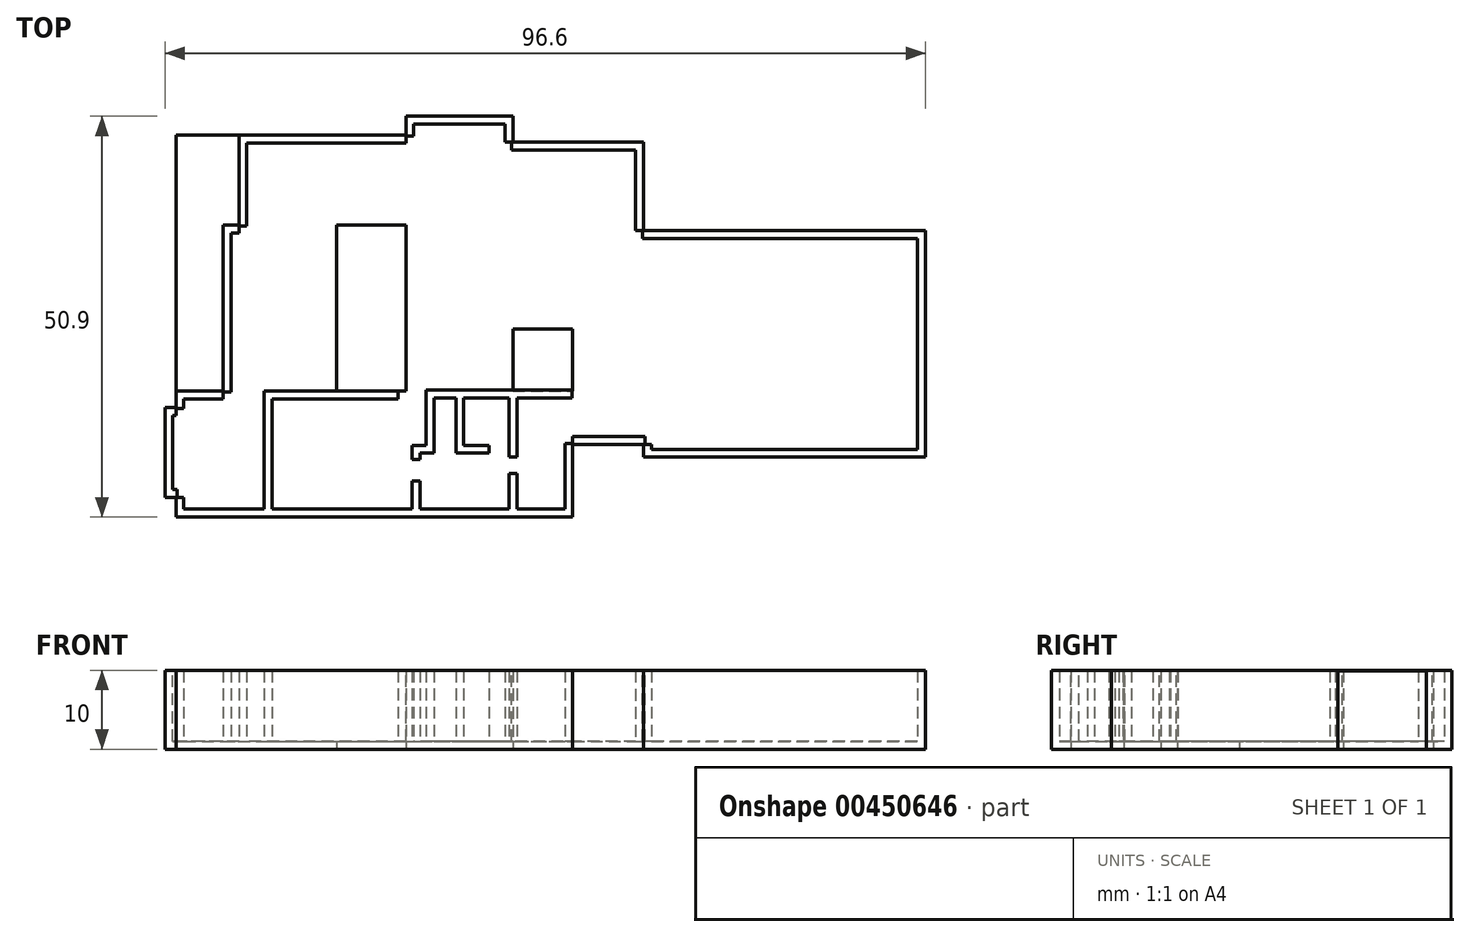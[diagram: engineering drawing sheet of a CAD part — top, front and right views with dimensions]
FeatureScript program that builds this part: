
annotation { "Feature Type Name" : "Feature", "Feature Type Description" : "" }
export const myFeature = defineFeature(function(context is Context, id is Id, definition is map)
    precondition{}
    {
        {
            var Q0;
            Q0=qCreatedBy(makeId("Top.planeOp"),FACE);
            var sketch = newSketch(context, id + "F0", { "sketchPlane" : qUnion([Q0])});
            skLineSegment(sketch, "E0.bottom", {"start": v(-51.63, -21.6) * mm, "end": v(-40.43, -21.6) * mm});
            skLineSegment(sketch, "E0.top", {"start": v(-51.63, -37.6) * mm, "end": v(-40.43, -37.6) * mm});
            skLineSegment(sketch, "E0.left", {"start": v(-51.63, -21.6) * mm, "end": v(-51.63, -37.6) * mm});
            skLineSegment(sketch, "E0.right", {"start": v(-40.43, -21.6) * mm, "end": v(-40.43, -37.6) * mm});
            skPoint(sketch, "E1.firstSnap0", {"position": v(-46.03, -21.6) * mm});
            skPoint(sketch, "E1.oppositeSnap0", {"position": v(-40.43, -29.6) * mm});
            skLineSegment(sketch, "E2.bottom", {"start": v(-51.63, -23.72) * mm, "end": v(-53.03, -23.72) * mm});
            skLineSegment(sketch, "E2.top", {"start": v(-51.63, -35.12) * mm, "end": v(-53.03, -35.12) * mm});
            skLineSegment(sketch, "E2.left", {"start": v(-51.63, -23.72) * mm, "end": v(-51.63, -35.12) * mm});
            skLineSegment(sketch, "E2.right", {"start": v(-53.03, -23.72) * mm, "end": v(-53.03, -35.12) * mm});
            skLineSegment(sketch, "E3.bottom", {"start": v(-45.63, -21.6) * mm, "end": v(-31.23, -21.6) * mm});
            skLineSegment(sketch, "E3.top", {"start": v(-45.63, -0.5) * mm, "end": v(-31.23, -0.5) * mm});
            skLineSegment(sketch, "E3.left", {"start": v(-45.63, -21.6) * mm, "end": v(-45.63, -0.5) * mm});
            skLineSegment(sketch, "E3.right", {"start": v(-31.23, -21.6) * mm, "end": v(-31.23, -0.5) * mm});
            skLineSegment(sketch, "E4.bottom", {"start": v(-43.63, -0.5) * mm, "end": v(-22.43, -0.5) * mm});
            skLineSegment(sketch, "E4.top", {"start": v(-43.63, 10.9) * mm, "end": v(-22.43, 10.9) * mm});
            skLineSegment(sketch, "E4.left", {"start": v(-43.63, -0.5) * mm, "end": v(-43.63, 10.9) * mm});
            skLineSegment(sketch, "E4.right", {"start": v(-22.43, -0.5) * mm, "end": v(-22.43, 10.9) * mm});
            skLineSegment(sketch, "E5.bottom", {"start": v(-22.43, 13.3) * mm, "end": v(-8.83, 13.3) * mm});
            skLineSegment(sketch, "E5.top", {"start": v(-22.43, -37.69) * mm, "end": v(-8.83, -37.69) * mm});
            skLineSegment(sketch, "E5.left", {"start": v(-22.43, 13.3) * mm, "end": v(-22.43, -37.69) * mm});
            skLineSegment(sketch, "E5.right", {"start": v(-8.83, 13.3) * mm, "end": v(-8.83, -37.69) * mm});
            skLineSegment(sketch, "E6.bottom", {"start": v(-8.83, 10) * mm, "end": v(7.77, 10) * mm});
            skLineSegment(sketch, "E6.top", {"start": v(-8.83, -13.72) * mm, "end": v(7.77, -13.72) * mm});
            skLineSegment(sketch, "E6.left", {"start": v(-8.83, 10) * mm, "end": v(-8.83, -13.72) * mm});
            skLineSegment(sketch, "E6.right", {"start": v(7.77, 10) * mm, "end": v(7.77, -13.72) * mm});
            skLineSegment(sketch, "E7.bottom", {"start": v(-51.63, -37.6) * mm, "end": v(-1.23, -37.6) * mm});
            skLineSegment(sketch, "E7.top", {"start": v(-51.63, -21.6) * mm, "end": v(-1.23, -21.6) * mm});
            skLineSegment(sketch, "E7.left", {"start": v(-51.63, -37.6) * mm, "end": v(-51.63, -21.6) * mm});
            skLineSegment(sketch, "E7.right", {"start": v(-1.23, -37.6) * mm, "end": v(-1.23, -21.6) * mm});
            skLineSegment(sketch, "E8.bottom", {"start": v(-1.23, -28.4) * mm, "end": v(7.77, -28.4) * mm});
            skLineSegment(sketch, "E8.top", {"start": v(-1.23, -13.72) * mm, "end": v(7.77, -13.72) * mm});
            skLineSegment(sketch, "E8.left", {"start": v(-1.23, -28.4) * mm, "end": v(-1.23, -13.72) * mm});
            skLineSegment(sketch, "E8.right", {"start": v(7.77, -28.4) * mm, "end": v(7.77, -13.72) * mm});
            skLineSegment(sketch, "E9.bottom", {"start": v(7.77, -30) * mm, "end": v(43.57, -30) * mm});
            skLineSegment(sketch, "E9.top", {"start": v(7.77, -1.2) * mm, "end": v(43.57, -1.2) * mm});
            skLineSegment(sketch, "E9.left", {"start": v(7.77, -30) * mm, "end": v(7.77, -1.2) * mm});
            skLineSegment(sketch, "E9.right", {"start": v(43.57, -30) * mm, "end": v(43.57, -1.2) * mm});
            skLineSegment(sketch, "E10.bottom", {"start": v(-31.23, -0.5) * mm, "end": v(-22.43, -0.5) * mm});
            skLineSegment(sketch, "E10.top", {"start": v(-31.23, -21.6) * mm, "end": v(-22.43, -21.6) * mm});
            skLineSegment(sketch, "E10.left", {"start": v(-31.23, -0.5) * mm, "end": v(-31.23, -21.6) * mm});
            skLineSegment(sketch, "E10.right", {"start": v(-22.43, -0.5) * mm, "end": v(-22.43, -21.6) * mm});
            skLineSegment(sketch, "E11.bottom", {"start": v(-1.23, -13.72) * mm, "end": v(-8.83, -13.72) * mm});
            skLineSegment(sketch, "E11.top", {"start": v(-1.23, -21.6) * mm, "end": v(-8.83, -21.6) * mm});
            skLineSegment(sketch, "E11.left", {"start": v(-1.23, -13.72) * mm, "end": v(-1.23, -21.6) * mm});
            skLineSegment(sketch, "E11.right", {"start": v(-8.83, -13.72) * mm, "end": v(-8.83, -21.6) * mm});
            skSolve(sketch);
        }
        {
            var Q0;
            Q0 = qSketchRegion(id + "F0", true);
            var Q1;
            Q1=makeQuery(id+"F0.imprint","IMPRINT",FACE,{"disambiguationData":[TD([[makeQuery(id+"F0.imprint","IMPRINT",EDGE,{"derivedFrom":sQuery(id+"F0.wireOp",EDGE,"E10.bottom")}),-1.0]])]});
            var Q2;
            Q2=makeQuery(id+"F0.imprint","IMPRINT",FACE,{"disambiguationData":[TD([[makeQuery(id+"F0.imprint","IMPRINT",EDGE,{"derivedFrom":sQuery(id+"F0.wireOp",EDGE,"E11.bottom")}),1.0]])]});
            extrude(context, id + "F1", {"entities" : qUnion([Q0, Q1, Q2]), "depth" : 1 * mm});
        }
        {
            var Q0;
            Q0=makeQuery(id+"F1.opExtrude","SWEPT_FACE",FACE,{"disambiguationData":[OSD([sQuery(id+"F0.wireOp",EDGE,"E2.right")])]});
            var sketch = newSketch(context, id + "F2", { "sketchPlane" : qUnion([Q0])});
            skLineSegment(sketch, "E12.bottom", {"start": v(23.72, 1) * mm, "end": v(35.12, 1) * mm});
            skLineSegment(sketch, "E12.top", {"start": v(23.72, 10) * mm, "end": v(35.12, 10) * mm});
            skLineSegment(sketch, "E12.left", {"start": v(23.72, 1) * mm, "end": v(23.72, 10) * mm});
            skLineSegment(sketch, "E12.right", {"start": v(35.12, 1) * mm, "end": v(35.12, 10) * mm});
            skSolve(sketch);
        }
        {
            var Q0;
            Q0 = qSketchRegion(id + "F2", true);
            extrude(context, id + "F3", {"entities" : qUnion([Q0]), "operationType" : NewBodyOperationType.ADD, "oppositeDirection" : true, "depth" : 1 * mm});
        }
        {
            var Q0;
            Q0=makeQuery(id+"F3.boolean.opBoolean","MERGE",FACE,{"derivedFrom":[makeQuery(id+"F1.opExtrude","SWEPT_FACE",FACE,{"disambiguationData":[OSD([sQuery(id+"F0.wireOp",EDGE,"E2.bottom")])]}),makeQuery(id+"F3.opExtrude","SWEPT_FACE",FACE,{"disambiguationData":[OSD([sQuery(id+"F2.wireOp",EDGE,"E12.left")])]})]});
            var sketch = newSketch(context, id + "F4", { "sketchPlane" : qUnion([Q0])});
            skLineSegment(sketch, "E13.bottom", {"start": v(51.63, 0) * mm, "end": v(53.03, 0) * mm});
            skLineSegment(sketch, "E13.top", {"start": v(51.63, 10) * mm, "end": v(53.03, 10) * mm});
            skLineSegment(sketch, "E13.left", {"start": v(51.63, 0) * mm, "end": v(51.63, 10) * mm});
            skLineSegment(sketch, "E13.right", {"start": v(53.03, 0) * mm, "end": v(53.03, 10) * mm});
            skSolve(sketch);
        }
        {
            var Q0;
            Q0 = qSketchRegion(id + "F4", true);
            extrude(context, id + "F5", {"entities" : qUnion([Q0]), "operationType" : NewBodyOperationType.ADD, "oppositeDirection" : true, "depth" : 1 * mm});
        }
        {
            var Q0;
            {var subQ0=sQuery(id+"F0.wireOp",EDGE,"E7.left");var subQ1=makeQuery(id+"F0.imprint","INTERSECT",VERTEX,{"derivedFrom":[sQuery(id+"F0.wireOp",EDGE,"E0.bottom"),subQ0]});Q0=makeQuery(id+"F1.opExtrude","SWEPT_FACE",FACE,{"disambiguationData":[OSD([subQ0]),TDD([makeQuery(id+"F0.imprint","IMPRINT",EDGE,{"disambiguationData":[TD([[subQ1,1.0]])],"derivedFrom":subQ0}),makeQuery(id+"F0.imprint","IMPRINT",EDGE,{"disambiguationData":[TD([[subQ1,-1.0]])],"derivedFrom":subQ0})])]});}
            var sketch = newSketch(context, id + "F6", { "sketchPlane" : qUnion([Q0])});
            skLineSegment(sketch, "E14.bottom", {"start": v(21.6, 0) * mm, "end": v(23.86, 0) * mm});
            skLineSegment(sketch, "E14.top", {"start": v(21.6, 10) * mm, "end": v(23.86, 10) * mm});
            skLineSegment(sketch, "E14.left", {"start": v(21.6, 0) * mm, "end": v(21.6, 10) * mm});
            skLineSegment(sketch, "E14.right", {"start": v(23.86, 0) * mm, "end": v(23.86, 10) * mm});
            skSolve(sketch);
        }
        {
            var Q0;
            Q0 = qSketchRegion(id + "F6", true);
            extrude(context, id + "F7", {"entities" : qUnion([Q0]), "operationType" : NewBodyOperationType.ADD, "oppositeDirection" : true, "depth" : 1 * mm});
        }
        {
            var Q0;
            Q0=makeQuery(id+"F7.boolean.opBoolean","MERGE",FACE,{"derivedFrom":[makeQuery(id+"F1.opExtrude","SWEPT_FACE",FACE,{"disambiguationData":[OSD([sQuery(id+"F0.wireOp",EDGE,"E7.top")])]}),makeQuery(id+"F7.opExtrude","SWEPT_FACE",FACE,{"disambiguationData":[OSD([sQuery(id+"F6.wireOp",EDGE,"E14.left")])]})]});
            var sketch = newSketch(context, id + "F8", { "sketchPlane" : qUnion([Q0])});
            skLineSegment(sketch, "E15.bottom", {"start": v(45.63, 0) * mm, "end": v(51.63, 0) * mm});
            skLineSegment(sketch, "E15.top", {"start": v(45.63, 10) * mm, "end": v(51.63, 10) * mm});
            skLineSegment(sketch, "E15.left", {"start": v(45.63, 0) * mm, "end": v(45.63, 10) * mm});
            skLineSegment(sketch, "E15.right", {"start": v(51.63, 0) * mm, "end": v(51.63, 10) * mm});
            skSolve(sketch);
        }
        {
            var Q0;
            Q0 = qSketchRegion(id + "F8", true);
            extrude(context, id + "F9", {"entities" : qUnion([Q0]), "operationType" : NewBodyOperationType.ADD, "oppositeDirection" : true, "depth" : 1 * mm});
        }
        {
            var Q0;
            Q0=makeQuery(id+"F1.opExtrude","SWEPT_FACE",FACE,{"disambiguationData":[OSD([sQuery(id+"F0.wireOp",EDGE,"E3.left")])]});
            var sketch = newSketch(context, id + "F10", { "sketchPlane" : qUnion([Q0])});
            skLineSegment(sketch, "E16.bottom", {"start": v(0.5, 0) * mm, "end": v(21.73, 0) * mm});
            skLineSegment(sketch, "E16.top", {"start": v(0.5, 10) * mm, "end": v(21.73, 10) * mm});
            skLineSegment(sketch, "E16.left", {"start": v(0.5, 0) * mm, "end": v(0.5, 10) * mm});
            skLineSegment(sketch, "E16.right", {"start": v(21.73, 0) * mm, "end": v(21.73, 10) * mm});
            skSolve(sketch);
        }
        {
            var Q0;
            Q0 = qSketchRegion(id + "F10", true);
            extrude(context, id + "F11", {"entities" : qUnion([Q0]), "operationType" : NewBodyOperationType.ADD, "oppositeDirection" : true, "depth" : 1 * mm});
        }
        {
            var Q0;
            Q0=makeQuery(id+"F11.boolean.opBoolean","MERGE",FACE,{"derivedFrom":[makeQuery(id+"F1.opExtrude","SWEPT_FACE",FACE,{"disambiguationData":[OSD([sQuery(id+"F0.wireOp",EDGE,"E3.top")])]}),makeQuery(id+"F11.opExtrude","SWEPT_FACE",FACE,{"disambiguationData":[OSD([sQuery(id+"F10.wireOp",EDGE,"E16.left")])]})]});
            var sketch = newSketch(context, id + "F12", { "sketchPlane" : qUnion([Q0])});
            skLineSegment(sketch, "E17.bottom", {"start": v(43.63, 0) * mm, "end": v(45.63, 0) * mm});
            skLineSegment(sketch, "E17.top", {"start": v(43.63, 10) * mm, "end": v(45.63, 10) * mm});
            skLineSegment(sketch, "E17.left", {"start": v(43.63, 0) * mm, "end": v(43.63, 10) * mm});
            skLineSegment(sketch, "E17.right", {"start": v(45.63, 0) * mm, "end": v(45.63, 10) * mm});
            skSolve(sketch);
        }
        {
            var Q0;
            Q0 = qSketchRegion(id + "F12", true);
            extrude(context, id + "F13", {"entities" : qUnion([Q0]), "operationType" : NewBodyOperationType.ADD, "oppositeDirection" : true, "depth" : 1 * mm});
        }
        {
            var Q0;
            Q0=makeQuery(id+"F1.opExtrude","SWEPT_FACE",FACE,{"disambiguationData":[OSD([sQuery(id+"F0.wireOp",EDGE,"E4.left")])]});
            var sketch = newSketch(context, id + "F14", { "sketchPlane" : qUnion([Q0])});
            skLineSegment(sketch, "E18.bottom", {"start": v(-10.9, 0) * mm, "end": v(0.63, 0) * mm});
            skLineSegment(sketch, "E18.top", {"start": v(-10.9, 10) * mm, "end": v(0.63, 10) * mm});
            skLineSegment(sketch, "E18.left", {"start": v(-10.9, 0) * mm, "end": v(-10.9, 10) * mm});
            skLineSegment(sketch, "E18.right", {"start": v(0.63, 0) * mm, "end": v(0.63, 10) * mm});
            skSolve(sketch);
        }
        {
            var Q0;
            Q0 = qSketchRegion(id + "F14", true);
            extrude(context, id + "F15", {"entities" : qUnion([Q0]), "operationType" : NewBodyOperationType.ADD, "oppositeDirection" : true, "depth" : 1 * mm});
        }
        {
            var Q0;
            Q0=makeQuery(id+"F15.boolean.opBoolean","MERGE",FACE,{"derivedFrom":[makeQuery(id+"F1.opExtrude","SWEPT_FACE",FACE,{"disambiguationData":[OSD([sQuery(id+"F0.wireOp",EDGE,"E4.top")])]}),makeQuery(id+"F15.opExtrude","SWEPT_FACE",FACE,{"disambiguationData":[OSD([sQuery(id+"F14.wireOp",EDGE,"E18.left")])]})]});
            var sketch = newSketch(context, id + "F16", { "sketchPlane" : qUnion([Q0])});
            skLineSegment(sketch, "E19.bottom", {"start": v(22.43, 0) * mm, "end": v(43.63, 0) * mm});
            skLineSegment(sketch, "E19.top", {"start": v(22.43, 10) * mm, "end": v(43.63, 10) * mm});
            skLineSegment(sketch, "E19.left", {"start": v(22.43, 0) * mm, "end": v(22.43, 10) * mm});
            skLineSegment(sketch, "E19.right", {"start": v(43.63, 0) * mm, "end": v(43.63, 10) * mm});
            skSolve(sketch);
        }
        {
            var Q0;
            Q0 = qSketchRegion(id + "F16", true);
            extrude(context, id + "F17", {"entities" : qUnion([Q0]), "operationType" : NewBodyOperationType.ADD, "oppositeDirection" : true, "depth" : 1 * mm});
        }
        {
            var Q0;
            {var subQ0=sQuery(id+"F0.wireOp",EDGE,"E5.left");Q0=makeQuery(id+"F1.opExtrude","SWEPT_FACE",FACE,{"disambiguationData":[OSD([subQ0]),TDD([makeQuery(id+"F0.imprint","IMPRINT",EDGE,{"disambiguationData":[TD([[makeQuery(id+"F0.imprint","INTERSECT",VERTEX,{"derivedFrom":[sQuery(id+"F0.wireOp",EDGE,"E4.top"),subQ0]}),1.0]])],"derivedFrom":subQ0})])]});}
            var sketch = newSketch(context, id + "F18", { "sketchPlane" : qUnion([Q0])});
            skLineSegment(sketch, "E20.bottom", {"start": v(-13.3, 0) * mm, "end": v(-10.8, 0) * mm});
            skLineSegment(sketch, "E20.top", {"start": v(-13.3, 10) * mm, "end": v(-10.8, 10) * mm});
            skLineSegment(sketch, "E20.left", {"start": v(-13.3, 0) * mm, "end": v(-13.3, 10) * mm});
            skLineSegment(sketch, "E20.right", {"start": v(-10.8, 0) * mm, "end": v(-10.8, 10) * mm});
            skSolve(sketch);
        }
        {
            var Q0;
            Q0 = qSketchRegion(id + "F18", true);
            extrude(context, id + "F19", {"entities" : qUnion([Q0]), "operationType" : NewBodyOperationType.ADD, "oppositeDirection" : true, "depth" : 1 * mm});
        }
        {
            var Q0;
            Q0=makeQuery(id+"F19.boolean.opBoolean","MERGE",FACE,{"derivedFrom":[makeQuery(id+"F1.opExtrude","SWEPT_FACE",FACE,{"disambiguationData":[OSD([sQuery(id+"F0.wireOp",EDGE,"E5.bottom")])]}),makeQuery(id+"F19.opExtrude","SWEPT_FACE",FACE,{"disambiguationData":[OSD([sQuery(id+"F18.wireOp",EDGE,"E20.left")])]})]});
            var sketch = newSketch(context, id + "F20", { "sketchPlane" : qUnion([Q0])});
            skLineSegment(sketch, "E21.bottom", {"start": v(22.43, 10) * mm, "end": v(8.83, 10) * mm});
            skLineSegment(sketch, "E21.top", {"start": v(22.43, 0) * mm, "end": v(8.83, 0) * mm});
            skLineSegment(sketch, "E21.left", {"start": v(22.43, 10) * mm, "end": v(22.43, 0) * mm});
            skLineSegment(sketch, "E21.right", {"start": v(8.83, 10) * mm, "end": v(8.83, 0) * mm});
            skSolve(sketch);
        }
        {
            var Q0;
            Q0 = qSketchRegion(id + "F20", true);
            extrude(context, id + "F21", {"entities" : qUnion([Q0]), "operationType" : NewBodyOperationType.ADD, "oppositeDirection" : true, "depth" : 1 * mm});
        }
        {
            var Q0;
            {var subQ0=sQuery(id+"F0.wireOp",EDGE,"E5.right");Q0=makeQuery(id+"F21.boolean.opBoolean","MERGE",FACE,{"derivedFrom":[makeQuery(id+"F1.opExtrude","SWEPT_FACE",FACE,{"disambiguationData":[OSD([subQ0]),TDD([makeQuery(id+"F0.imprint","IMPRINT",EDGE,{"disambiguationData":[TD([[makeQuery(id+"F0.imprint","INTERSECT",VERTEX,{"derivedFrom":[sQuery(id+"F0.wireOp",EDGE,"E5.bottom"),subQ0]}),-1.0]])],"derivedFrom":subQ0})])]}),makeQuery(id+"F21.opExtrude","SWEPT_FACE",FACE,{"disambiguationData":[OSD([sQuery(id+"F20.wireOp",EDGE,"E21.right")])]})]});}
            var sketch = newSketch(context, id + "F22", { "sketchPlane" : qUnion([Q0])});
            skLineSegment(sketch, "E22.bottom", {"start": v(10, 0) * mm, "end": v(13.3, 0) * mm});
            skLineSegment(sketch, "E22.top", {"start": v(10, 10) * mm, "end": v(13.3, 10) * mm});
            skLineSegment(sketch, "E22.left", {"start": v(10, 0) * mm, "end": v(10, 10) * mm});
            skLineSegment(sketch, "E22.right", {"start": v(13.3, 0) * mm, "end": v(13.3, 10) * mm});
            skSolve(sketch);
        }
        {
            var Q0;
            Q0 = qSketchRegion(id + "F22", true);
            extrude(context, id + "F23", {"entities" : qUnion([Q0]), "operationType" : NewBodyOperationType.ADD, "oppositeDirection" : true, "depth" : 1 * mm});
        }
        {
            var Q0;
            Q0=makeQuery(id+"F1.opExtrude","SWEPT_FACE",FACE,{"disambiguationData":[OSD([sQuery(id+"F0.wireOp",EDGE,"E6.bottom")])]});
            var sketch = newSketch(context, id + "F24", { "sketchPlane" : qUnion([Q0])});
            skLineSegment(sketch, "E23.bottom", {"start": v(-7.77, 0) * mm, "end": v(8.99, 0) * mm});
            skLineSegment(sketch, "E23.top", {"start": v(-7.77, 9.96) * mm, "end": v(8.99, 9.96) * mm});
            skLineSegment(sketch, "E23.left", {"start": v(-7.77, 0) * mm, "end": v(-7.77, 9.96) * mm});
            skLineSegment(sketch, "E23.right", {"start": v(8.99, 0) * mm, "end": v(8.99, 9.96) * mm});
            skSolve(sketch);
        }
        {
            var Q0;
            Q0 = qSketchRegion(id + "F24", true);
            extrude(context, id + "F25", {"entities" : qUnion([Q0]), "operationType" : NewBodyOperationType.ADD, "oppositeDirection" : true, "depth" : 1 * mm});
        }
        {
            var Q0;
            Q0=makeQuery(id+"F25.boolean.opBoolean","MERGE",FACE,{"derivedFrom":[makeQuery(id+"F1.opExtrude","SWEPT_FACE",FACE,{"disambiguationData":[OSD([sQuery(id+"F0.wireOp",EDGE,"E6.right")])]}),makeQuery(id+"F25.opExtrude","SWEPT_FACE",FACE,{"disambiguationData":[OSD([sQuery(id+"F24.wireOp",EDGE,"E23.left")])]})]});
            var sketch = newSketch(context, id + "F26", { "sketchPlane" : qUnion([Q0])});
            skLineSegment(sketch, "E24.bottom", {"start": v(-1.2, 0) * mm, "end": v(10, 0) * mm});
            skLineSegment(sketch, "E24.top", {"start": v(-1.2, 9.96) * mm, "end": v(10, 9.96) * mm});
            skLineSegment(sketch, "E24.left", {"start": v(-1.2, 0) * mm, "end": v(-1.2, 9.96) * mm});
            skLineSegment(sketch, "E24.right", {"start": v(10, 0) * mm, "end": v(10, 9.96) * mm});
            skSolve(sketch);
        }
        {
            var Q0;
            Q0 = qSketchRegion(id + "F26", true);
            extrude(context, id + "F27", {"entities" : qUnion([Q0]), "operationType" : NewBodyOperationType.ADD, "oppositeDirection" : true, "depth" : 1 * mm});
        }
        {
            var Q0;
            Q0=makeQuery(id+"F1.opExtrude","SWEPT_FACE",FACE,{"disambiguationData":[OSD([sQuery(id+"F0.wireOp",EDGE,"E9.top")])]});
            var sketch = newSketch(context, id + "F28", { "sketchPlane" : qUnion([Q0])});
            skLineSegment(sketch, "E25.bottom", {"start": v(-43.57, 0) * mm, "end": v(-7.6, 0) * mm});
            skLineSegment(sketch, "E25.top", {"start": v(-43.57, 10) * mm, "end": v(-7.6, 10) * mm});
            skLineSegment(sketch, "E25.left", {"start": v(-43.57, 0) * mm, "end": v(-43.57, 10) * mm});
            skLineSegment(sketch, "E25.right", {"start": v(-7.6, 0) * mm, "end": v(-7.6, 10) * mm});
            skSolve(sketch);
        }
        {
            var Q0;
            Q0 = qSketchRegion(id + "F28", true);
            extrude(context, id + "F29", {"entities" : qUnion([Q0]), "operationType" : NewBodyOperationType.ADD, "oppositeDirection" : true, "depth" : 1 * mm});
        }
        {
            var Q0;
            Q0=makeQuery(id+"F29.boolean.opBoolean","MERGE",FACE,{"derivedFrom":[makeQuery(id+"F1.opExtrude","SWEPT_FACE",FACE,{"disambiguationData":[OSD([sQuery(id+"F0.wireOp",EDGE,"E9.right")])]}),makeQuery(id+"F29.opExtrude","SWEPT_FACE",FACE,{"disambiguationData":[OSD([sQuery(id+"F28.wireOp",EDGE,"E25.left")])]})]});
            var sketch = newSketch(context, id + "F30", { "sketchPlane" : qUnion([Q0])});
            skLineSegment(sketch, "E26.bottom", {"start": v(-30, 0) * mm, "end": v(-1.2, 0) * mm});
            skLineSegment(sketch, "E26.top", {"start": v(-30, 10) * mm, "end": v(-1.2, 10) * mm});
            skLineSegment(sketch, "E26.left", {"start": v(-30, 0) * mm, "end": v(-30, 10) * mm});
            skLineSegment(sketch, "E26.right", {"start": v(-1.2, 0) * mm, "end": v(-1.2, 10) * mm});
            skSolve(sketch);
        }
        {
            var Q0;
            Q0 = qSketchRegion(id + "F30", true);
            extrude(context, id + "F31", {"entities" : qUnion([Q0]), "operationType" : NewBodyOperationType.ADD, "oppositeDirection" : true, "depth" : 1 * mm});
        }
        {
            var Q0;
            Q0=makeQuery(id+"F31.boolean.opBoolean","MERGE",FACE,{"derivedFrom":[makeQuery(id+"F1.opExtrude","SWEPT_FACE",FACE,{"disambiguationData":[OSD([sQuery(id+"F0.wireOp",EDGE,"E9.bottom")])]}),makeQuery(id+"F31.opExtrude","SWEPT_FACE",FACE,{"disambiguationData":[OSD([sQuery(id+"F30.wireOp",EDGE,"E26.left")])]})]});
            var sketch = newSketch(context, id + "F32", { "sketchPlane" : qUnion([Q0])});
            skLineSegment(sketch, "E27.bottom", {"start": v(7.77, 0) * mm, "end": v(43.57, 0) * mm});
            skLineSegment(sketch, "E27.top", {"start": v(7.77, 10) * mm, "end": v(43.57, 10) * mm});
            skLineSegment(sketch, "E27.left", {"start": v(7.77, 0) * mm, "end": v(7.77, 10) * mm});
            skLineSegment(sketch, "E27.right", {"start": v(43.57, 0) * mm, "end": v(43.57, 10) * mm});
            skSolve(sketch);
        }
        {
            var Q0;
            Q0 = qSketchRegion(id + "F32", true);
            extrude(context, id + "F33", {"entities" : qUnion([Q0]), "operationType" : NewBodyOperationType.ADD, "oppositeDirection" : true, "depth" : 1 * mm});
        }
        {
            var Q0;
            Q0=makeQuery(id+"F33.boolean.opBoolean","MERGE",FACE,{"derivedFrom":[makeQuery(id+"F1.opExtrude","SWEPT_FACE",FACE,{"disambiguationData":[OSD([sQuery(id+"F0.wireOp",EDGE,"E9.left")])]}),makeQuery(id+"F33.opExtrude","SWEPT_FACE",FACE,{"disambiguationData":[OSD([sQuery(id+"F32.wireOp",EDGE,"E27.left")])]})]});
            var sketch = newSketch(context, id + "F34", { "sketchPlane" : qUnion([Q0])});
            skLineSegment(sketch, "E28.bottom", {"start": v(28.4, 0) * mm, "end": v(30, 0) * mm});
            skLineSegment(sketch, "E28.top", {"start": v(28.4, 10) * mm, "end": v(30, 10) * mm});
            skLineSegment(sketch, "E28.left", {"start": v(28.4, 0) * mm, "end": v(28.4, 10) * mm});
            skLineSegment(sketch, "E28.right", {"start": v(30, 0) * mm, "end": v(30, 10) * mm});
            skSolve(sketch);
        }
        {
            var Q0;
            Q0 = qSketchRegion(id + "F34", true);
            extrude(context, id + "F35", {"entities" : qUnion([Q0]), "operationType" : NewBodyOperationType.ADD, "oppositeDirection" : true, "depth" : 1 * mm});
        }
        {
            var Q0;
            Q0=makeQuery(id+"F1.opExtrude","SWEPT_FACE",FACE,{"disambiguationData":[OSD([sQuery(id+"F0.wireOp",EDGE,"E8.bottom")])]});
            var sketch = newSketch(context, id + "F36", { "sketchPlane" : qUnion([Q0])});
            skLineSegment(sketch, "E29.bottom", {"start": v(-1.23, 0) * mm, "end": v(7.96, 0) * mm});
            skLineSegment(sketch, "E29.top", {"start": v(-1.23, 10) * mm, "end": v(7.96, 10) * mm});
            skLineSegment(sketch, "E29.left", {"start": v(-1.23, 0) * mm, "end": v(-1.23, 10) * mm});
            skLineSegment(sketch, "E29.right", {"start": v(7.96, 0) * mm, "end": v(7.96, 10) * mm});
            skSolve(sketch);
        }
        {
            var Q0;
            Q0 = qSketchRegion(id + "F36", true);
            extrude(context, id + "F37", {"entities" : qUnion([Q0]), "operationType" : NewBodyOperationType.ADD, "oppositeDirection" : true, "depth" : 1 * mm});
        }
        {
            var Q0;
            Q0=makeQuery(id+"F1.opExtrude","SWEPT_FACE",FACE,{"disambiguationData":[OSD([sQuery(id+"F0.wireOp",EDGE,"E7.right")])]});
            var sketch = newSketch(context, id + "F38", { "sketchPlane" : qUnion([Q0])});
            skLineSegment(sketch, "E30.bottom", {"start": v(-37.6, 0) * mm, "end": v(-28.28, 0) * mm});
            skLineSegment(sketch, "E30.top", {"start": v(-37.6, 10) * mm, "end": v(-28.28, 10) * mm});
            skLineSegment(sketch, "E30.left", {"start": v(-37.6, 0) * mm, "end": v(-37.6, 10) * mm});
            skLineSegment(sketch, "E30.right", {"start": v(-28.28, 0) * mm, "end": v(-28.28, 10) * mm});
            skSolve(sketch);
        }
        {
            var Q0;
            Q0 = qSketchRegion(id + "F38", true);
            extrude(context, id + "F39", {"entities" : qUnion([Q0]), "operationType" : NewBodyOperationType.ADD, "oppositeDirection" : true, "depth" : 1 * mm});
        }
        {
            var Q0;
            {var subQ0=sQuery(id+"F0.wireOp",EDGE,"E7.bottom");var subQ1=makeQuery(id+"F0.imprint","INTERSECT",VERTEX,{"derivedFrom":[sQuery(id+"F0.wireOp",EDGE,"E0.right"),subQ0]});Q0=makeQuery(id+"F1.opExtrude","SWEPT_FACE",FACE,{"disambiguationData":[OSD([subQ0]),TDD([makeQuery(id+"F0.imprint","IMPRINT",EDGE,{"disambiguationData":[TD([[subQ1,1.0]])],"derivedFrom":subQ0}),makeQuery(id+"F0.imprint","IMPRINT",EDGE,{"disambiguationData":[TD([[subQ1,-1.0]])],"derivedFrom":subQ0})])]});}
            var sketch = newSketch(context, id + "F40", { "sketchPlane" : qUnion([Q0])});
            skLineSegment(sketch, "E31.bottom", {"start": v(-51.63, 0) * mm, "end": v(-1.72, 0) * mm});
            skLineSegment(sketch, "E31.top", {"start": v(-51.63, 10) * mm, "end": v(-1.72, 10) * mm});
            skLineSegment(sketch, "E31.left", {"start": v(-51.63, 0) * mm, "end": v(-51.63, 10) * mm});
            skLineSegment(sketch, "E31.right", {"start": v(-1.72, 0) * mm, "end": v(-1.72, 10) * mm});
            skSolve(sketch);
        }
        {
            var Q0;
            Q0 = qSketchRegion(id + "F40", true);
            extrude(context, id + "F41", {"entities" : qUnion([Q0]), "operationType" : NewBodyOperationType.ADD, "oppositeDirection" : true, "depth" : 1 * mm});
        }
        {
            var Q0;
            {var subQ0=sQuery(id+"F0.wireOp",EDGE,"E7.bottom");var subQ1=makeQuery(id+"F0.imprint","INTERSECT",VERTEX,{"derivedFrom":[sQuery(id+"F0.wireOp",EDGE,"E0.right"),subQ0]});Q0=makeQuery(id+"F41.boolean.opBoolean","MERGE",FACE,{"derivedFrom":[makeQuery(id+"F1.opExtrude","SWEPT_FACE",FACE,{"disambiguationData":[OSD([subQ0]),TDD([makeQuery(id+"F0.imprint","IMPRINT",EDGE,{"disambiguationData":[TD([[subQ1,1.0]])],"derivedFrom":subQ0}),makeQuery(id+"F0.imprint","IMPRINT",EDGE,{"disambiguationData":[TD([[subQ1,-1.0]])],"derivedFrom":subQ0})])]}),makeQuery(id+"F39.boolean.opBoolean","MERGE",FACE,{"derivedFrom":[makeQuery(id+"F1.opExtrude","SWEPT_FACE",FACE,{"disambiguationData":[OSD([subQ0]),TDD([makeQuery(id+"F0.imprint","IMPRINT",EDGE,{"disambiguationData":[TD([[makeQuery(id+"F0.imprint","INTERSECT",VERTEX,{"derivedFrom":[subQ0,sQuery(id+"F0.wireOp",EDGE,"E7.right")]}),1.0]])],"derivedFrom":subQ0})])]}),makeQuery(id+"F39.opExtrude","SWEPT_FACE",FACE,{"disambiguationData":[OSD([sQuery(id+"F38.wireOp",EDGE,"E30.left")])]})]}),makeQuery(id+"F41.opExtrude","CAP_FACE",FACE,{"disambiguationData":[OSD([sQuery(id+"F40.wireOp",EDGE,"E31.bottom"),sQuery(id+"F40.wireOp",EDGE,"E31.top"),sQuery(id+"F40.wireOp",EDGE,"E31.left"),sQuery(id+"F40.wireOp",EDGE,"E31.right")])],"isStart":true})]});}
            var sketch = newSketch(context, id + "F42", { "sketchPlane" : qUnion([Q0])});
            skLineSegment(sketch, "E32.bottom", {"start": v(-51.63, 0) * mm, "end": v(-1.23, 0) * mm});
            skLineSegment(sketch, "E32.top", {"start": v(-51.63, 10) * mm, "end": v(-1.23, 10) * mm});
            skLineSegment(sketch, "E32.left", {"start": v(-51.63, 0) * mm, "end": v(-51.63, 10) * mm});
            skLineSegment(sketch, "E32.right", {"start": v(-1.23, 0) * mm, "end": v(-1.23, 10) * mm});
            skSolve(sketch);
        }
        {
            var Q0;
            Q0 = qSketchRegion(id + "F42", true);
            extrude(context, id + "F43", {"entities" : qUnion([Q0]), "operationType" : NewBodyOperationType.REMOVE, "depth" : 25.4 * mm});
        }
        {
            var Q0;
            {var subQ0=sQuery(id+"F0.wireOp",EDGE,"E7.left");Q0=makeQuery(id+"F41.boolean.opBoolean","MERGE",FACE,{"derivedFrom":[makeQuery(id+"F1.opExtrude","SWEPT_FACE",FACE,{"disambiguationData":[OSD([subQ0]),TDD([makeQuery(id+"F0.imprint","IMPRINT",EDGE,{"disambiguationData":[TD([[makeQuery(id+"F0.imprint","INTERSECT",VERTEX,{"derivedFrom":[sQuery(id+"F0.wireOp",EDGE,"E2.top"),subQ0]}),1.0]])],"derivedFrom":subQ0})])]}),makeQuery(id+"F41.opExtrude","SWEPT_FACE",FACE,{"disambiguationData":[OSD([sQuery(id+"F40.wireOp",EDGE,"E31.left")])]})]});}
            var sketch = newSketch(context, id + "F44", { "sketchPlane" : qUnion([Q0])});
            skLineSegment(sketch, "E33.bottom", {"start": v(35.12, 0) * mm, "end": v(37.6, 0) * mm});
            skLineSegment(sketch, "E33.top", {"start": v(35.12, 10) * mm, "end": v(37.6, 10) * mm});
            skLineSegment(sketch, "E33.left", {"start": v(35.12, 0) * mm, "end": v(35.12, 10) * mm});
            skLineSegment(sketch, "E33.right", {"start": v(37.6, 0) * mm, "end": v(37.6, 10) * mm});
            skSolve(sketch);
        }
        {
            var Q0;
            Q0 = qSketchRegion(id + "F44", true);
            extrude(context, id + "F45", {"entities" : qUnion([Q0]), "operationType" : NewBodyOperationType.ADD, "oppositeDirection" : true, "depth" : 1 * mm});
        }
        {
            var Q0;
            Q0=makeQuery(id+"F3.boolean.opBoolean","MERGE",FACE,{"derivedFrom":[makeQuery(id+"F1.opExtrude","SWEPT_FACE",FACE,{"disambiguationData":[OSD([sQuery(id+"F0.wireOp",EDGE,"E2.top")])]}),makeQuery(id+"F3.opExtrude","SWEPT_FACE",FACE,{"disambiguationData":[OSD([sQuery(id+"F2.wireOp",EDGE,"E12.right")])]})]});
            var sketch = newSketch(context, id + "F46", { "sketchPlane" : qUnion([Q0])});
            skLineSegment(sketch, "E34.bottom", {"start": v(-53.03, 0) * mm, "end": v(-51.5, 0) * mm});
            skLineSegment(sketch, "E34.top", {"start": v(-53.03, 10) * mm, "end": v(-51.5, 10) * mm});
            skLineSegment(sketch, "E34.left", {"start": v(-53.03, 0) * mm, "end": v(-53.03, 10) * mm});
            skLineSegment(sketch, "E34.right", {"start": v(-51.5, 0) * mm, "end": v(-51.5, 10) * mm});
            skSolve(sketch);
        }
        {
            var Q0;
            Q0 = qSketchRegion(id + "F46", true);
            extrude(context, id + "F47", {"entities" : qUnion([Q0]), "operationType" : NewBodyOperationType.ADD, "oppositeDirection" : true, "depth" : 1 * mm});
        }
        {
            var Q0;
            Q0=qCreatedBy(makeId("Top.planeOp"),FACE);
            var sketch = newSketch(context, id + "F48", { "sketchPlane" : qUnion([Q0])});
            skLineSegment(sketch, "E35.bottom", {"start": v(-43.63, 10.9) * mm, "end": v(-51.63, 10.9) * mm});
            skLineSegment(sketch, "E35.top", {"start": v(-43.63, -21.6) * mm, "end": v(-51.63, -21.6) * mm});
            skLineSegment(sketch, "E35.left", {"start": v(-43.63, 10.9) * mm, "end": v(-43.63, -21.6) * mm});
            skLineSegment(sketch, "E35.right", {"start": v(-51.63, 10.9) * mm, "end": v(-51.63, -21.6) * mm});
            skSolve(sketch);
        }
        {
            var Q0;
            Q0 = qSketchRegion(id + "F48", true);
            extrude(context, id + "F49", {"entities" : qUnion([Q0]), "operationType" : NewBodyOperationType.ADD, "depth" : 1 * mm});
        }
        {
            var Q0;
            {var subQ7=sQuery(id+"F0.wireOp",EDGE,"E2.top");var subQ10=sQuery(id+"F0.wireOp",EDGE,"E7.left");var subQ11=sQuery(id+"F0.wireOp",EDGE,"E7.bottom");Q0=makeQuery(id+"F41.boolean.opBoolean","SPLIT",FACE,{"disambiguationData":[TD([makeQuery(id+"F1.opExtrude","SWEPT_FACE",FACE,{"disambiguationData":[OSD([subQ7])]})])],"derivedFrom":makeQuery(id+"F1.opExtrude","CAP_FACE",FACE,{"disambiguationData":[OSD([sQuery(id+"F0.wireOp",EDGE,"E2.bottom"),subQ7,sQuery(id+"F0.wireOp",EDGE,"E2.right"),sQuery(id+"F0.wireOp",EDGE,"E3.top"),sQuery(id+"F0.wireOp",EDGE,"E3.left"),sQuery(id+"F0.wireOp",EDGE,"E4.top"),sQuery(id+"F0.wireOp",EDGE,"E4.left"),sQuery(id+"F0.wireOp",EDGE,"E5.bottom"),sQuery(id+"F0.wireOp",EDGE,"E5.top"),sQuery(id+"F0.wireOp",EDGE,"E5.left"),sQuery(id+"F0.wireOp",EDGE,"E5.right"),sQuery(id+"F0.wireOp",EDGE,"E6.bottom"),sQuery(id+"F0.wireOp",EDGE,"E6.right"),subQ11,sQuery(id+"F0.wireOp",EDGE,"E7.top"),subQ10,sQuery(id+"F0.wireOp",EDGE,"E7.right"),sQuery(id+"F0.wireOp",EDGE,"E8.bottom"),sQuery(id+"F0.wireOp",EDGE,"E9.bottom"),sQuery(id+"F0.wireOp",EDGE,"E9.top"),sQuery(id+"F0.wireOp",EDGE,"E9.left"),sQuery(id+"F0.wireOp",EDGE,"E9.right")])],"isStart":false})});}
            var sketch = newSketch(context, id + "F50", { "sketchPlane" : qUnion([Q0])});
            skLineSegment(sketch, "E36.bottom", {"start": v(-40.43, -37.6) * mm, "end": v(-39.43, -37.6) * mm});
            skLineSegment(sketch, "E36.top", {"start": v(-40.43, -21.6) * mm, "end": v(-39.43, -21.6) * mm});
            skLineSegment(sketch, "E36.left", {"start": v(-40.43, -37.6) * mm, "end": v(-40.43, -21.6) * mm});
            skLineSegment(sketch, "E36.right", {"start": v(-39.43, -37.6) * mm, "end": v(-39.43, -21.6) * mm});
            skLineSegment(sketch, "E37.bottom", {"start": v(-21.63, -37.6) * mm, "end": v(-20.63, -37.6) * mm});
            skLineSegment(sketch, "E37.top", {"start": v(-21.63, -28.5) * mm, "end": v(-20.63, -28.5) * mm});
            skLineSegment(sketch, "E37.left", {"start": v(-21.63, -37.6) * mm, "end": v(-21.63, -28.5) * mm});
            skLineSegment(sketch, "E37.right", {"start": v(-20.63, -37.6) * mm, "end": v(-20.63, -28.5) * mm});
            skLineSegment(sketch, "E38.bottom", {"start": v(-40.43, -21.6) * mm, "end": v(-23.45, -21.6) * mm});
            skLineSegment(sketch, "E38.top", {"start": v(-40.43, -22.6) * mm, "end": v(-23.45, -22.6) * mm});
            skLineSegment(sketch, "E38.left", {"start": v(-40.43, -21.6) * mm, "end": v(-40.43, -22.6) * mm});
            skLineSegment(sketch, "E38.right", {"start": v(-23.45, -21.6) * mm, "end": v(-23.45, -22.6) * mm});
            skLineSegment(sketch, "E39.bottom", {"start": v(-9.33, -37.6) * mm, "end": v(-8.33, -37.6) * mm});
            skLineSegment(sketch, "E39.top", {"start": v(-9.33, -22.4) * mm, "end": v(-8.33, -22.4) * mm});
            skLineSegment(sketch, "E39.left", {"start": v(-9.33, -37.6) * mm, "end": v(-9.33, -22.4) * mm});
            skLineSegment(sketch, "E39.right", {"start": v(-8.33, -37.6) * mm, "end": v(-8.33, -22.4) * mm});
            skLineSegment(sketch, "E40.bottom", {"start": v(-21.63, -28.5) * mm, "end": v(-18.83, -28.5) * mm});
            skLineSegment(sketch, "E40.top", {"start": v(-21.63, -29.5) * mm, "end": v(-18.83, -29.5) * mm});
            skLineSegment(sketch, "E40.left", {"start": v(-21.63, -28.5) * mm, "end": v(-21.63, -29.5) * mm});
            skLineSegment(sketch, "E40.right", {"start": v(-18.83, -28.5) * mm, "end": v(-18.83, -29.5) * mm});
            skLineSegment(sketch, "E41.bottom", {"start": v(-18.83, -28.5) * mm, "end": v(-19.83, -28.5) * mm});
            skLineSegment(sketch, "E41.top", {"start": v(-18.83, -21.5) * mm, "end": v(-19.83, -21.5) * mm});
            skLineSegment(sketch, "E41.left", {"start": v(-18.83, -28.5) * mm, "end": v(-18.83, -21.5) * mm});
            skLineSegment(sketch, "E41.right", {"start": v(-19.83, -28.5) * mm, "end": v(-19.83, -21.5) * mm});
            skLineSegment(sketch, "E42.bottom", {"start": v(-19.83, -21.5) * mm, "end": v(-8.33, -21.5) * mm});
            skLineSegment(sketch, "E42.top", {"start": v(-19.83, -22.5) * mm, "end": v(-8.33, -22.5) * mm});
            skLineSegment(sketch, "E42.left", {"start": v(-19.83, -21.5) * mm, "end": v(-19.83, -22.5) * mm});
            skLineSegment(sketch, "E42.right", {"start": v(-8.33, -21.5) * mm, "end": v(-8.33, -22.5) * mm});
            skLineSegment(sketch, "E43.bottom", {"start": v(-16.08, -21.5) * mm, "end": v(-15.08, -21.5) * mm});
            skLineSegment(sketch, "E43.top", {"start": v(-16.08, -29.5) * mm, "end": v(-15.08, -29.5) * mm});
            skLineSegment(sketch, "E43.left", {"start": v(-16.08, -21.5) * mm, "end": v(-16.08, -29.5) * mm});
            skLineSegment(sketch, "E43.right", {"start": v(-15.08, -21.5) * mm, "end": v(-15.08, -29.5) * mm});
            skLineSegment(sketch, "E44.bottom", {"start": v(-16.08, -29.5) * mm, "end": v(-11.88, -29.5) * mm});
            skLineSegment(sketch, "E44.top", {"start": v(-16.08, -28.5) * mm, "end": v(-11.88, -28.5) * mm});
            skLineSegment(sketch, "E44.left", {"start": v(-16.08, -29.5) * mm, "end": v(-16.08, -28.5) * mm});
            skLineSegment(sketch, "E44.right", {"start": v(-11.88, -29.5) * mm, "end": v(-11.88, -28.5) * mm});
            skLineSegment(sketch, "E45.bottom", {"start": v(-9.33, -30) * mm, "end": v(-8.33, -30) * mm});
            skLineSegment(sketch, "E45.top", {"start": v(-9.33, -32.1) * mm, "end": v(-8.33, -32.1) * mm});
            skLineSegment(sketch, "E45.left", {"start": v(-9.33, -30) * mm, "end": v(-9.33, -32.1) * mm});
            skLineSegment(sketch, "E45.right", {"start": v(-8.33, -30) * mm, "end": v(-8.33, -32.1) * mm});
            skLineSegment(sketch, "E46.bottom", {"start": v(-8.33, -21.5) * mm, "end": v(-1.33, -21.5) * mm});
            skLineSegment(sketch, "E46.top", {"start": v(-8.33, -22.5) * mm, "end": v(-1.33, -22.5) * mm});
            skLineSegment(sketch, "E46.right", {"start": v(-1.33, -21.5) * mm, "end": v(-1.33, -22.5) * mm});
            skLineSegment(sketch, "E47.bottom", {"start": v(-21.63, -30.3) * mm, "end": v(-20.63, -30.3) * mm});
            skLineSegment(sketch, "E47.top", {"start": v(-21.63, -33.06) * mm, "end": v(-20.63, -33.06) * mm});
            skLineSegment(sketch, "E47.left", {"start": v(-21.63, -30.3) * mm, "end": v(-21.63, -33.06) * mm});
            skLineSegment(sketch, "E47.right", {"start": v(-20.63, -30.3) * mm, "end": v(-20.63, -33.06) * mm});
            skSolve(sketch);
        }
        {
            var Q0;
            Q0 = qSketchRegion(id + "F50", true);
            extrude(context, id + "F51", {"entities" : qUnion([Q0]), "operationType" : NewBodyOperationType.ADD, "depth" : 9 * mm});
        }
        {
            var Q0;
            Q0=makeQuery(id+"F50.imprint","IMPRINT",FACE,{"disambiguationData":[TD([[makeQuery(id+"F50.imprint","IMPRINT",EDGE,{"derivedFrom":sQuery(id+"F50.wireOp",EDGE,"E47.bottom")}),-1.0]])]});
            extrude(context, id + "F52", {"entities" : qUnion([Q0]), "operationType" : NewBodyOperationType.REMOVE, "depth" : 9 * mm});
        }
        {
            var Q0;
            Q0=makeQuery(id+"F50.imprint","IMPRINT",FACE,{"disambiguationData":[TD([[makeQuery(id+"F50.imprint","IMPRINT",EDGE,{"derivedFrom":sQuery(id+"F50.wireOp",EDGE,"E45.bottom")}),-1.0]])]});
            extrude(context, id + "F53", {"entities" : qUnion([Q0]), "operationType" : NewBodyOperationType.REMOVE, "depth" : 9 * mm});
        }
    });
